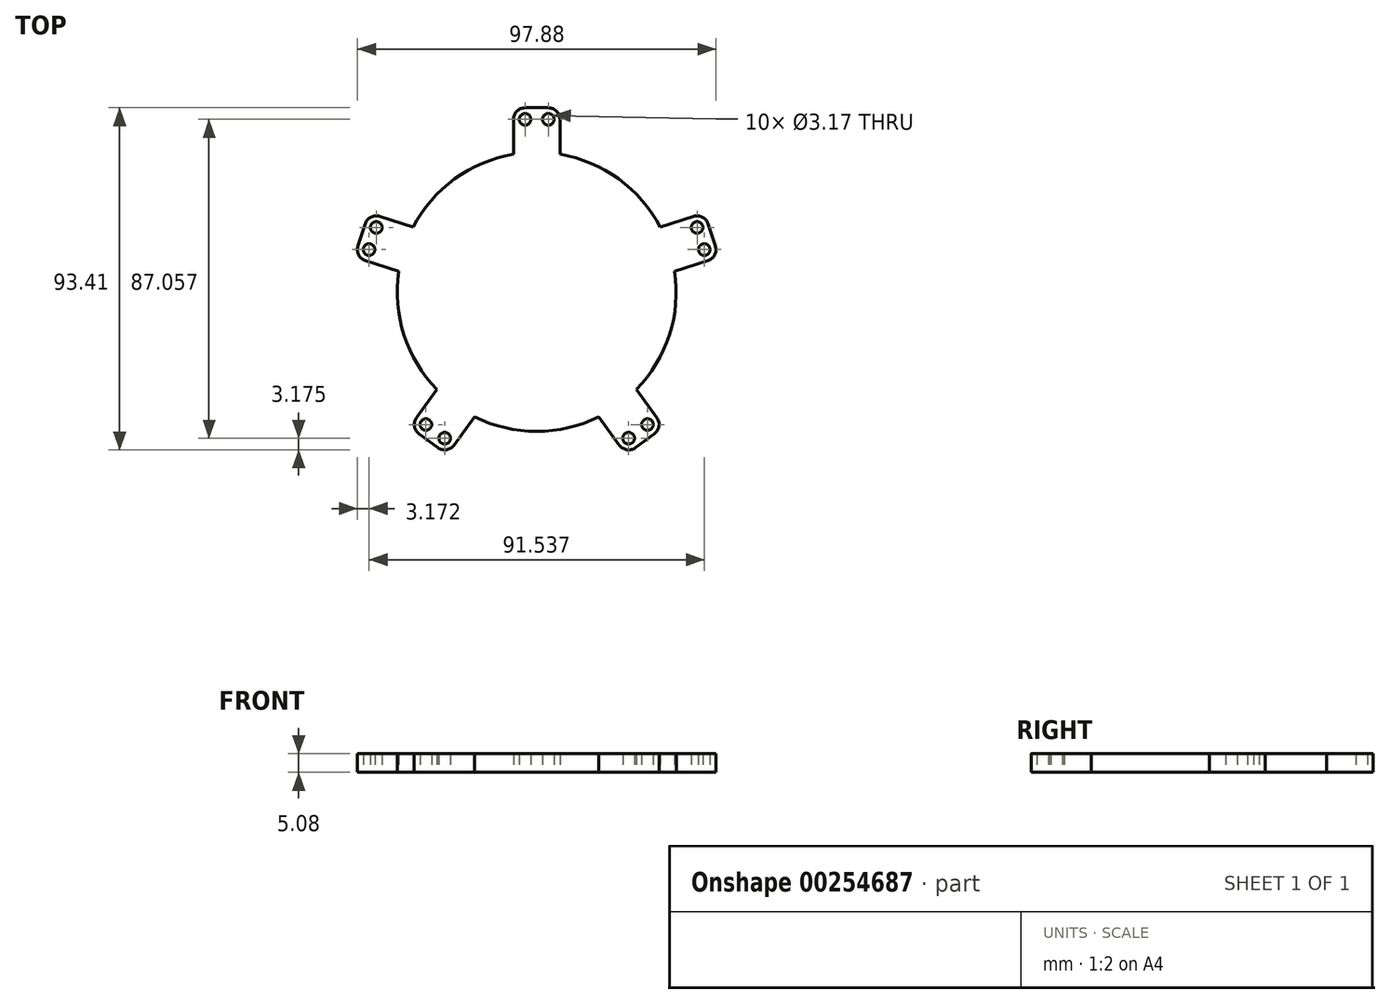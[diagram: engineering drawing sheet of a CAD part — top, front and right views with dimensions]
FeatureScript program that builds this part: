
annotation { "Feature Type Name" : "Feature", "Feature Type Description" : "" }
export const myFeature = defineFeature(function(context is Context, id is Id, definition is map)
    precondition{}
    {
        {
            var Q0;
            Q0=qCreatedBy(makeId("Top.planeOp"),FACE);
            var sketch = newSketch(context, id + "F0", { "sketchPlane" : qUnion([Q0])});
            skCircle(sketch, "E0", {"center": v(0, 0) * mm, "radius": 38.1 * mm});
            skLineSegment(sketch, "E1", {"start": v(-6.35, 37.57) * mm, "end": v(-6.35, 47.1) * mm});
            skLineSegment(sketch, "E2", {"start": v(0, 0) * mm, "end": v(0, 134.39) * mm, "construction": true});
            skLineSegment(sketch, "E3.MirrorCS", {"start": v(6.35, 37.57) * mm, "end": v(6.35, 47.1) * mm});
            skLineSegment(sketch, "E4", {"start": v(-3.17, 50.27) * mm, "end": v(3.18, 50.27) * mm});
            skCircle(sketch, "E5", {"center": v(-3.18, 47.1) * mm, "radius": 1.59 * mm});
            skCircle(sketch, "E6.MirrorC", {"center": v(3.18, 47.1) * mm, "radius": 1.59 * mm});
            skPoint(sketch, "E7.visualSharp", {"position": v(-6.35, 50.27) * mm});
            skArc(sketch, "E7.filletArc", {"start": v(-3.17, 50.27) * mm, "mid": v(-5.42, 49.34) * mm, "end": v(-6.35, 47.1) * mm});
            skPoint(sketch, "E8.1.0", {"position": v(-49.77, 9.5) * mm});
            skLineSegment(sketch, "E8.1.1", {"start": v(-33.77, 17.65) * mm, "end": v(-42.82, 20.6) * mm});
            skLineSegment(sketch, "E8.1.2", {"start": v(-37.7, 5.57) * mm, "end": v(-46.75, 8.51) * mm});
            skLineSegment(sketch, "E8.1.3", {"start": v(-48.79, 12.51) * mm, "end": v(-46.83, 18.55) * mm});
            skCircle(sketch, "E8.1.4", {"center": v(-43.8, 17.57) * mm, "radius": 1.59 * mm});
            skCircle(sketch, "E8.1.5", {"center": v(-45.77, 11.53) * mm, "radius": 1.59 * mm});
            skArc(sketch, "E8.1.6", {"start": v(-48.79, 12.51) * mm, "mid": v(-48.6, 10.1) * mm, "end": v(-46.75, 8.51) * mm});
            skPoint(sketch, "E8.2.0", {"position": v(-24.4, -44.4) * mm});
            skLineSegment(sketch, "E8.2.1", {"start": v(-27.22, -26.66) * mm, "end": v(-32.82, -34.37) * mm});
            skLineSegment(sketch, "E8.2.2", {"start": v(-16.94, -34.12) * mm, "end": v(-22.54, -41.83) * mm});
            skLineSegment(sketch, "E8.2.3", {"start": v(-26.98, -42.53) * mm, "end": v(-32.11, -38.8) * mm});
            skCircle(sketch, "E8.2.4", {"center": v(-30.25, -36.23) * mm, "radius": 1.59 * mm});
            skCircle(sketch, "E8.2.5", {"center": v(-25.11, -39.96) * mm, "radius": 1.59 * mm});
            skArc(sketch, "E8.2.6", {"start": v(-26.98, -42.53) * mm, "mid": v(-24.61, -43.1) * mm, "end": v(-22.54, -41.83) * mm});
            skPoint(sketch, "E8.3.0", {"position": v(34.68, -36.93) * mm});
            skLineSegment(sketch, "E8.3.1", {"start": v(16.94, -34.12) * mm, "end": v(22.54, -41.83) * mm});
            skLineSegment(sketch, "E8.3.2", {"start": v(27.22, -26.66) * mm, "end": v(32.82, -34.37) * mm});
            skLineSegment(sketch, "E8.3.3", {"start": v(32.11, -38.8) * mm, "end": v(26.98, -42.53) * mm});
            skCircle(sketch, "E8.3.4", {"center": v(25.11, -39.96) * mm, "radius": 1.59 * mm});
            skCircle(sketch, "E8.3.5", {"center": v(30.25, -36.23) * mm, "radius": 1.59 * mm});
            skArc(sketch, "E8.3.6", {"start": v(32.11, -38.8) * mm, "mid": v(33.38, -36.73) * mm, "end": v(32.82, -34.37) * mm});
            skPoint(sketch, "E8.4.0", {"position": v(45.84, 21.57) * mm});
            skLineSegment(sketch, "E8.4.1", {"start": v(37.7, 5.57) * mm, "end": v(46.75, 8.51) * mm});
            skLineSegment(sketch, "E8.4.2", {"start": v(33.77, 17.65) * mm, "end": v(42.82, 20.6) * mm});
            skLineSegment(sketch, "E8.4.3", {"start": v(46.83, 18.55) * mm, "end": v(48.79, 12.51) * mm});
            skCircle(sketch, "E8.4.4", {"center": v(45.77, 11.53) * mm, "radius": 1.59 * mm});
            skCircle(sketch, "E8.4.5", {"center": v(43.8, 17.57) * mm, "radius": 1.59 * mm});
            skArc(sketch, "E8.4.6", {"start": v(46.83, 18.55) * mm, "mid": v(45.25, 20.4) * mm, "end": v(42.82, 20.6) * mm});
            skPoint(sketch, "E9.visualSharp", {"position": v(-45.84, 21.57) * mm});
            skArc(sketch, "E9.filletArc", {"start": v(-42.82, 20.6) * mm, "mid": v(-45.25, 20.4) * mm, "end": v(-46.83, 18.55) * mm});
            skPoint(sketch, "E10.visualSharp", {"position": v(49.77, 9.5) * mm});
            skArc(sketch, "E10.filletArc", {"start": v(46.75, 8.51) * mm, "mid": v(48.6, 10.1) * mm, "end": v(48.79, 12.51) * mm});
            skPoint(sketch, "E11.visualSharp", {"position": v(24.4, -44.4) * mm});
            skArc(sketch, "E11.filletArc", {"start": v(22.54, -41.83) * mm, "mid": v(24.61, -43.1) * mm, "end": v(26.98, -42.53) * mm});
            skPoint(sketch, "E12.visualSharp", {"position": v(-34.68, -36.93) * mm});
            skArc(sketch, "E12.filletArc", {"start": v(-32.82, -34.37) * mm, "mid": v(-33.38, -36.73) * mm, "end": v(-32.11, -38.8) * mm});
            skPoint(sketch, "E13.visualSharp", {"position": v(6.35, 50.27) * mm});
            skArc(sketch, "E13.filletArc", {"start": v(6.35, 47.1) * mm, "mid": v(5.42, 49.34) * mm, "end": v(3.18, 50.27) * mm});
            skSolve(sketch);
        }
        {
            var Q0;
            Q0 = qSketchRegion(id + "F0", true);
            extrude(context, id + "F1", {"entities" : qUnion([Q0]), "depth" : 5.08 * mm});
        }
        {
            var Q0;
            Q0 = qSketchRegion(id + "F0", true);
            extrude(context, id + "F2", {"entities" : qUnion([Q0]), "operationType" : NewBodyOperationType.REMOVE, "oppositeDirection" : true, "depth" : 5.08 * mm});
        }
    });
